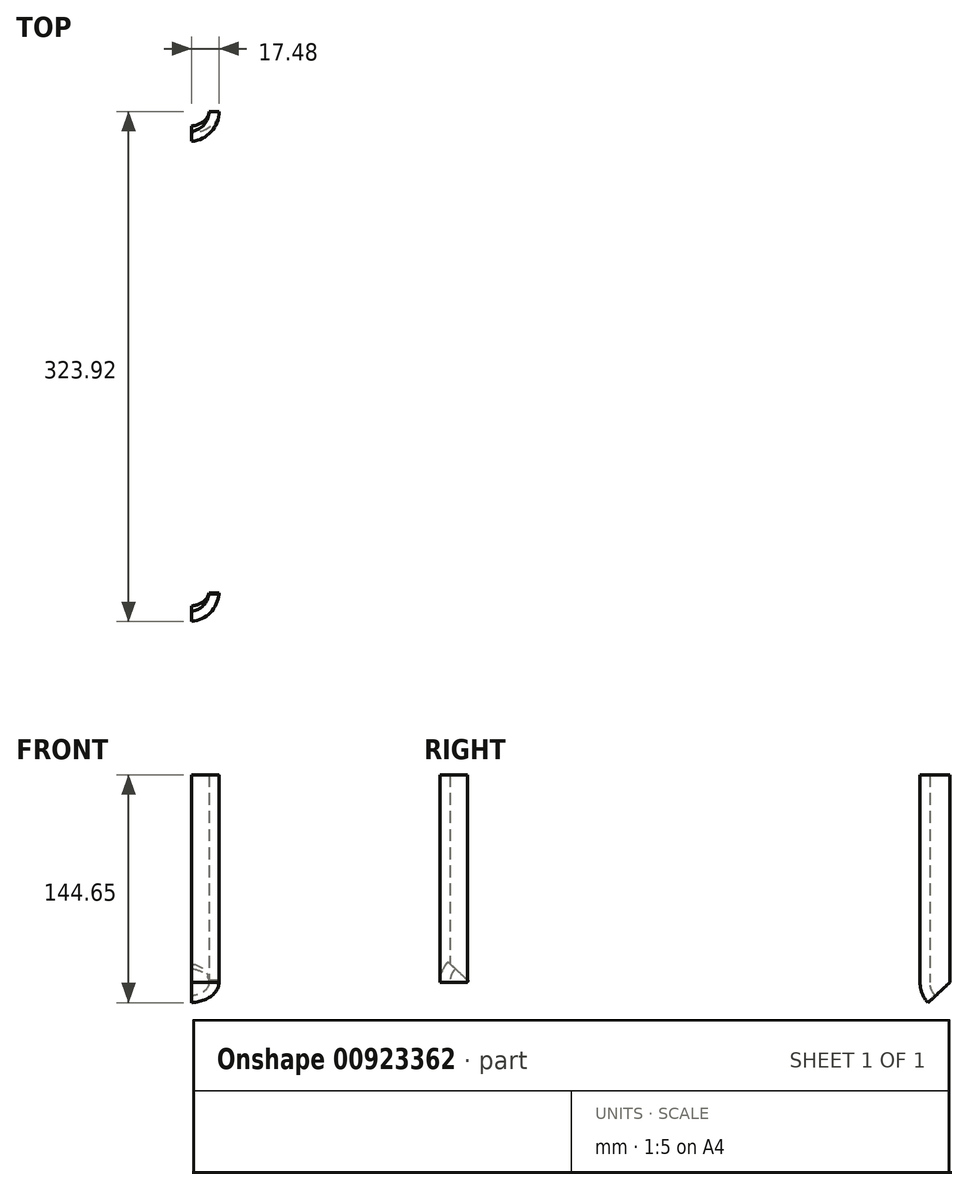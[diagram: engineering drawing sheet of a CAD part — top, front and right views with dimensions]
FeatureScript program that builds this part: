
annotation { "Feature Type Name" : "Feature", "Feature Type Description" : "" }
export const myFeature = defineFeature(function(context is Context, id is Id, definition is map)
    precondition{}
    {
        {
            var Q0;
            Q0=qCreatedBy(makeId("Top.planeOp"),FACE);
            var sketch = newSketch(context, id + "F0", { "sketchPlane" : qUnion([Q0])});
            skCircle(sketch, "E0", {"center": v(0, 0) * mm, "radius": 19.05 * mm});
            skCircle(sketch, "E1", {"center": v(0, 0) * mm, "radius": 12.7 * mm});
            skLineSegment(sketch, "E2", {"start": v(0, 26) * mm, "end": v(0, -46.34) * mm});
            skLineSegment(sketch, "E3", {"start": v(-25.03, 0) * mm, "end": v(32.81, 0.18) * mm});
            skLineSegment(sketch, "E4.0", {"start": v(-25.03, -1.59) * mm, "end": v(32.82, -1.4) * mm});
            skLineSegment(sketch, "E5.0", {"start": v(-25.04, 1.59) * mm, "end": v(32.8, 1.77) * mm});
            skLineSegment(sketch, "E6.0", {"start": v(-1.59, 26) * mm, "end": v(-1.59, -46.34) * mm});
            skLineSegment(sketch, "E7.0", {"start": v(1.59, 26) * mm, "end": v(1.59, -46.34) * mm});
            skSolve(sketch);
        }
        {
            var Q0;
            {var subQ0=sQuery(id+"F0.wireOp",EDGE,"E5.0");var subQ1=sQuery(id+"F0.wireOp",EDGE,"E0");var subQ2=makeQuery(id+"F0.imprint","INTERSECT",VERTEX,{"disambiguationData":[OD(0.0)],"derivedFrom":[subQ1,subQ0]});Q0=makeQuery(id+"F0.imprint","IMPRINT",FACE,{"disambiguationData":[TD([[makeQuery(id+"F0.imprint","IMPRINT",EDGE,{"disambiguationData":[TD([[subQ2,-1.0]])],"derivedFrom":subQ1}),1.0]])]});}
            extrude(context, id + "F1", {"entities" : qUnion([Q0]), "depth" : 149.22 * mm - 19.05 * mm, "offsetDistance" : 30.48 * mm});
        }
        {
            var Q0;
            Q0=makeQuery(id+"F1.opExtrude","CAP_FACE",FACE,{"disambiguationData":[OSD([sQuery(id+"F0.wireOp",EDGE,"E0"),sQuery(id+"F0.wireOp",EDGE,"E1"),sQuery(id+"F0.wireOp",EDGE,"E5.0"),sQuery(id+"F0.wireOp",EDGE,"E7.0")])],"isStart":false});
            extrude(context, id + "F2", {"entities" : qUnion([Q0]), "depth" : 1.59 * mm, "offsetDistance" : 30.48 * mm});
        }
        {
            var Q0;
            {var subQ0=sQuery(id+"F0.wireOp",EDGE,"E7.0");var subQ1=sQuery(id+"F0.wireOp",EDGE,"E0");var subQ2=makeQuery(id+"F0.imprint","INTERSECT",VERTEX,{"disambiguationData":[OD(0.0)],"derivedFrom":[subQ1,subQ0]});Q0=makeQuery(id+"F0.imprint","IMPRINT",FACE,{"disambiguationData":[TD([[makeQuery(id+"F0.imprint","IMPRINT",EDGE,{"disambiguationData":[TD([[subQ2,-1.0]])],"derivedFrom":subQ1}),1.0]])]});}
            var Q1;
            {var subQ0=sQuery(id+"F0.wireOp",EDGE,"E5.0");var subQ1=sQuery(id+"F0.wireOp",EDGE,"E0");var subQ2=makeQuery(id+"F0.imprint","INTERSECT",VERTEX,{"disambiguationData":[OD(0.0)],"derivedFrom":[subQ1,subQ0]});Q1=makeQuery(id+"F0.imprint","IMPRINT",FACE,{"disambiguationData":[TD([[makeQuery(id+"F0.imprint","IMPRINT",EDGE,{"disambiguationData":[TD([[subQ2,1.0]])],"derivedFrom":subQ1}),1.0]])]});}
            extrude(context, id + "F3", {"entities" : qUnion([Q0, Q1]), "operationType" : NewBodyOperationType.ADD, "depth" : 150.8 * mm - 19.05 * mm, "offsetDistance" : 30.48 * mm});
        }
        {
            var Q0;
            Q0=makeQuery(id+"F3.opExtrude","CAP_FACE",FACE,{"disambiguationData":[OSD([sQuery(id+"F0.wireOp",EDGE,"E0"),sQuery(id+"F0.wireOp",EDGE,"E1"),sQuery(id+"F0.wireOp",EDGE,"E3"),sQuery(id+"F0.wireOp",EDGE,"E5.0")])],"isStart":true});
            var Q1;
            Q1=makeQuery(id+"F1.opExtrude","CAP_FACE",FACE,{"disambiguationData":[OSD([sQuery(id+"F0.wireOp",EDGE,"E0"),sQuery(id+"F0.wireOp",EDGE,"E1"),sQuery(id+"F0.wireOp",EDGE,"E5.0"),sQuery(id+"F0.wireOp",EDGE,"E7.0")])],"isStart":true});
            var Q2;
            Q2=makeQuery(id+"F3.opExtrude","CAP_FACE",FACE,{"disambiguationData":[OSD([sQuery(id+"F0.wireOp",EDGE,"E0"),sQuery(id+"F0.wireOp",EDGE,"E1"),sQuery(id+"F0.wireOp",EDGE,"E2"),sQuery(id+"F0.wireOp",EDGE,"E7.0")])],"isStart":true});
            var Q3;
            Q3=makeQuery(id+"F3.opExtrude","CAP_EDGE",EDGE,{"disambiguationData":[OSD([sQuery(id+"F0.wireOp",EDGE,"E3")])],"isStart":true});
            revolve(context, id + "F4", {"operationType" : NewBodyOperationType.ADD, "surfaceOperationType" : NewSurfaceOperationType.NEW, "entities" : qUnion([Q0, Q1, Q2]), "axis" : qUnion([Q3]), "revolveType" : RevolveType.ONE_DIRECTION, "oppositeDirection" : true, "angle" : 43 * degree});
        }
        {
            var Q0;
            Q0=makeQuery(id+"F2.opExtrude","SWEPT_BODY",BODY,{"disambiguationData":[OSD([sQuery(id+"F0.wireOp",EDGE,"E0"),sQuery(id+"F0.wireOp",EDGE,"E1"),sQuery(id+"F0.wireOp",EDGE,"E5.0"),sQuery(id+"F0.wireOp",EDGE,"E7.0")])]});
            var Q1;
            Q1=makeQuery(id+"F1.opExtrude","SWEPT_BODY",BODY,{"disambiguationData":[OSD([sQuery(id+"F0.wireOp",EDGE,"E0"),sQuery(id+"F0.wireOp",EDGE,"E1"),sQuery(id+"F0.wireOp",EDGE,"E5.0"),sQuery(id+"F0.wireOp",EDGE,"E7.0")])]});
            var Q2;
            Q2=makeQuery(id+"F3.opExtrude","SWEPT_FACE",FACE,{"disambiguationData":[OSD([sQuery(id+"F0.wireOp",EDGE,"E3")])]});
            mirror(context, id + "F5", {"entities" : qUnion([Q0, Q1]), "mirrorPlane" : qUnion([Q2])});
        }
        {
            var Q0;
            Q0=makeQuery(id+"F5.opPattern","COPY",BODY,{"derivedFrom":makeQuery(id+"F1.opExtrude","SWEPT_BODY",BODY,{"disambiguationData":[OSD([sQuery(id+"F0.wireOp",EDGE,"E0"),sQuery(id+"F0.wireOp",EDGE,"E1"),sQuery(id+"F0.wireOp",EDGE,"E5.0"),sQuery(id+"F0.wireOp",EDGE,"E7.0")])]}),"instanceName":"1"});
            var Q1;
            Q1=makeQuery(id+"F5.opPattern","COPY",BODY,{"derivedFrom":makeQuery(id+"F2.opExtrude","SWEPT_BODY",BODY,{"disambiguationData":[OSD([sQuery(id+"F0.wireOp",EDGE,"E0"),sQuery(id+"F0.wireOp",EDGE,"E1"),sQuery(id+"F0.wireOp",EDGE,"E5.0"),sQuery(id+"F0.wireOp",EDGE,"E7.0")])]}),"instanceName":"1"});
            transform(context, id + "F6", {"entities" : qUnion([Q0, Q1]), "transformType" : TransformType.TRANSLATION_3D, "dx" : 0 * mm, "dy" : 304.8 * mm, "dz" : 0 * mm, "makeCopy" : true});
        }
        {
            var Q0;
            Q0=makeQuery(id+"F2.opExtrude","SWEPT_BODY",BODY,{"disambiguationData":[OSD([sQuery(id+"F0.wireOp",EDGE,"E0"),sQuery(id+"F0.wireOp",EDGE,"E1"),sQuery(id+"F0.wireOp",EDGE,"E5.0"),sQuery(id+"F0.wireOp",EDGE,"E7.0")])]});
            var Q1;
            Q1=makeQuery(id+"F1.opExtrude","SWEPT_BODY",BODY,{"disambiguationData":[OSD([sQuery(id+"F0.wireOp",EDGE,"E0"),sQuery(id+"F0.wireOp",EDGE,"E1"),sQuery(id+"F0.wireOp",EDGE,"E5.0"),sQuery(id+"F0.wireOp",EDGE,"E7.0")])]});
            var Q2;
            Q2=makeQuery(id+"F5.opPattern","COPY",BODY,{"derivedFrom":makeQuery(id+"F1.opExtrude","SWEPT_BODY",BODY,{"disambiguationData":[OSD([sQuery(id+"F0.wireOp",EDGE,"E0"),sQuery(id+"F0.wireOp",EDGE,"E1"),sQuery(id+"F0.wireOp",EDGE,"E5.0"),sQuery(id+"F0.wireOp",EDGE,"E7.0")])]}),"instanceName":"1"});
            var Q3;
            Q3=makeQuery(id+"F5.opPattern","COPY",BODY,{"derivedFrom":makeQuery(id+"F2.opExtrude","SWEPT_BODY",BODY,{"disambiguationData":[OSD([sQuery(id+"F0.wireOp",EDGE,"E0"),sQuery(id+"F0.wireOp",EDGE,"E1"),sQuery(id+"F0.wireOp",EDGE,"E5.0"),sQuery(id+"F0.wireOp",EDGE,"E7.0")])]}),"instanceName":"1"});
            deleteBodies(context, id + "F7", {"entities" : qUnion([Q0, Q1, Q2, Q3])});
        }
    });
